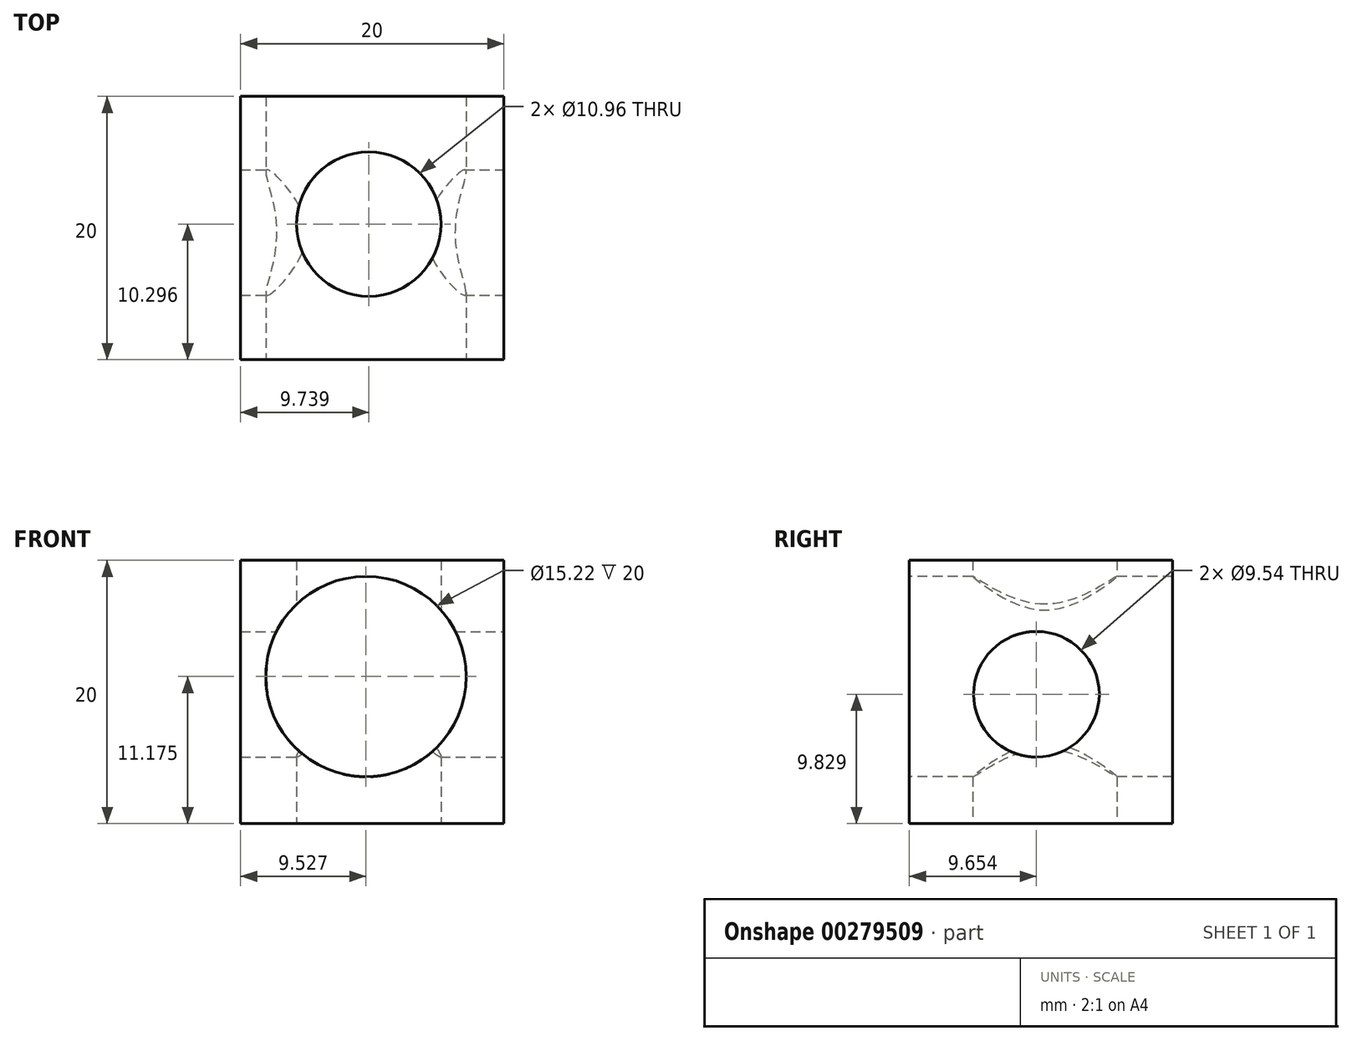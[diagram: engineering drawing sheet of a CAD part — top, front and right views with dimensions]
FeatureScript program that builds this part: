
annotation { "Feature Type Name" : "Feature", "Feature Type Description" : "" }
export const myFeature = defineFeature(function(context is Context, id is Id, definition is map)
    precondition{}
    {
        {
            var Q0;
            Q0=qCreatedBy(makeId("Top.planeOp"),FACE);
            var sketch = newSketch(context, id + "F0", { "sketchPlane" : qUnion([Q0])});
            skLineSegment(sketch, "E0.bottom", {"start": v(0, 0) * mm, "end": v(20, 0) * mm});
            skLineSegment(sketch, "E0.top", {"start": v(0, 20) * mm, "end": v(20, 20) * mm});
            skLineSegment(sketch, "E0.left", {"start": v(0, 0) * mm, "end": v(0, 20) * mm});
            skLineSegment(sketch, "E0.right", {"start": v(20, 0) * mm, "end": v(20, 20) * mm});
            skSolve(sketch);
        }
        {
            var Q0;
            Q0=makeQuery(id+"F0.imprint","IMPRINT",FACE,{"disambiguationData":[TD([[makeQuery(id+"F0.imprint","IMPRINT",EDGE,{"derivedFrom":sQuery(id+"F0.wireOp",EDGE,"E0.bottom")}),1.0]])]});
            extrude(context, id + "F1", {"entities" : qUnion([Q0]), "depth" : 20 * mm});
        }
        {
            var Q0;
            Q0=qCreatedBy(makeId("Top.planeOp"),FACE);
            var sketch = newSketch(context, id + "F2", { "sketchPlane" : qUnion([Q0])});
            skCircle(sketch, "E1", {"center": v(9.74, 10.3) * mm, "radius": 5.48 * mm});
            skSolve(sketch);
        }
        {
            var Q0;
            Q0 = qSketchRegion(id + "F2", true);
            var Q1;
            Q1=makeQuery(id+"F1.opExtrude","CAP_FACE",FACE,{"disambiguationData":[OSD([sQuery(id+"F0.wireOp",EDGE,"E0.bottom"),sQuery(id+"F0.wireOp",EDGE,"E0.top"),sQuery(id+"F0.wireOp",EDGE,"E0.left"),sQuery(id+"F0.wireOp",EDGE,"E0.right")])],"isStart":false});
            extrude(context, id + "F3", {"entities" : qUnion([Q0, Q1]), "operationType" : NewBodyOperationType.REMOVE, "depth" : 20 * mm});
        }
        {
            var Q0;
            Q0=makeQuery(id+"F1.opExtrude","SWEPT_FACE",FACE,{"disambiguationData":[OSD([sQuery(id+"F0.wireOp",EDGE,"E0.right")])]});
            var sketch = newSketch(context, id + "F4", { "sketchPlane" : qUnion([Q0])});
            skCircle(sketch, "E2", {"center": v(9.65, 9.83) * mm, "radius": 4.77 * mm});
            skSolve(sketch);
        }
        {
            var Q0;
            Q0 = qSketchRegion(id + "F4", true);
            var Q1;
            Q1=makeQuery(id+"F1.opExtrude","SWEPT_FACE",FACE,{"disambiguationData":[OSD([sQuery(id+"F0.wireOp",EDGE,"E0.left")])]});
            extrude(context, id + "F5", {"entities" : qUnion([Q0, Q1]), "operationType" : NewBodyOperationType.REMOVE, "oppositeDirection" : true, "depth" : 20 * mm});
        }
        {
            var Q0;
            Q0=makeQuery(id+"F1.opExtrude","SWEPT_FACE",FACE,{"disambiguationData":[OSD([sQuery(id+"F0.wireOp",EDGE,"E0.bottom")])]});
            var sketch = newSketch(context, id + "F6", { "sketchPlane" : qUnion([Q0])});
            skCircle(sketch, "E3", {"center": v(9.53, 11.17) * mm, "radius": 7.61 * mm});
            skSolve(sketch);
        }
        {
            var Q0;
            Q0 = qSketchRegion(id + "F6", true);
            extrude(context, id + "F7", {"entities" : qUnion([Q0]), "operationType" : NewBodyOperationType.REMOVE, "oppositeDirection" : true, "depth" : 20 * mm});
        }
    });
